# Revit family: Forniture_Stool_Plank_Blocco-Stool
name_source: partatom
category: Furniture
revit_build: Autodesk Revit 2017 (Build: 20160225_1515(x64)
units: mm (PartAtom-declared; Revit-internal decimal feet)

## family parameters
Cut with Voids When Loaded = No
Host = Face
Room Calculation Point = No
Shared = No

## types (2) — shared parameters
BIMobject category = Chairs, Stools & Benches
BIMobject category code = furniture-chairs-stools-benches
BIMobject main category = Furniture
BIMobject main category code = furniture
Brand url = http://www.plank.it
Default Elevation = 1219 mm
Design country = Italy
Edition number = 1
IFC Classification = Furnishing Element
Link Model = https://www.plank.it
Manufacturer country = Italy
Manufacturer name = PLANK
Masterformat 2014 Code = 12 00 00
Masterformat 2014 Description = Furnishings
Material main = Wood
Material secondary = Paint
NBS Reference Code = 31
NBS Reference Description = Fittings, Furnishings And Equipment (Ff&E) Products
OmniClass Code = 23-21 00 00
OmniClass Description = Furnishings, Fixtures and Equipment Products
Product Guid = 7a3048ce-f884-49dc-8f50-27b34def9914
Product SKU = Blocco-Stool
Product data url = https://bimobject.com
Product family = Blocco
Product group = Stool
Product url = https://www.plank.it
QR code = http://bimobject.com
Ring = Plank - Aluminum
Technical description = https://www.plank.it
UNSPSC Code = 56
URL = https://www.plank.it
Uniclass 1.4 Code = JN
Uniclass 1.4 Description = Furniture/Equipment
Uniclass 2.0 Code = EE-35
Uniclass 2.0 Description = Fittings, Furnishings And Equipment (Ff&E) And Signage Elements
Uniclass 2015 Code = EF_40_30
Uniclass 2015 Name = Furnishings
Uniformat II Code = E2020
Uniformat II Description = Movable Furnishings
Weight Net (Kg) = 0
structure = Plank-Frassino
zero-valued in all types: Nominal height, Nominal width

## per-type parameters (varying)
| type | Hight stool |
| Blocco Stool- Mod. 8500-00 (76 cm) | 760 mm |
| Blocco Stool - Mod. 8500-60 (63 cm) | 630 mm  [stored 2.06693 ft] |

note: column(s) folded — value = type name in every type: Model

note: [stored X ft] marks values corroborated as IEEE doubles in the binary element streams (Revit-internal decimal feet)
